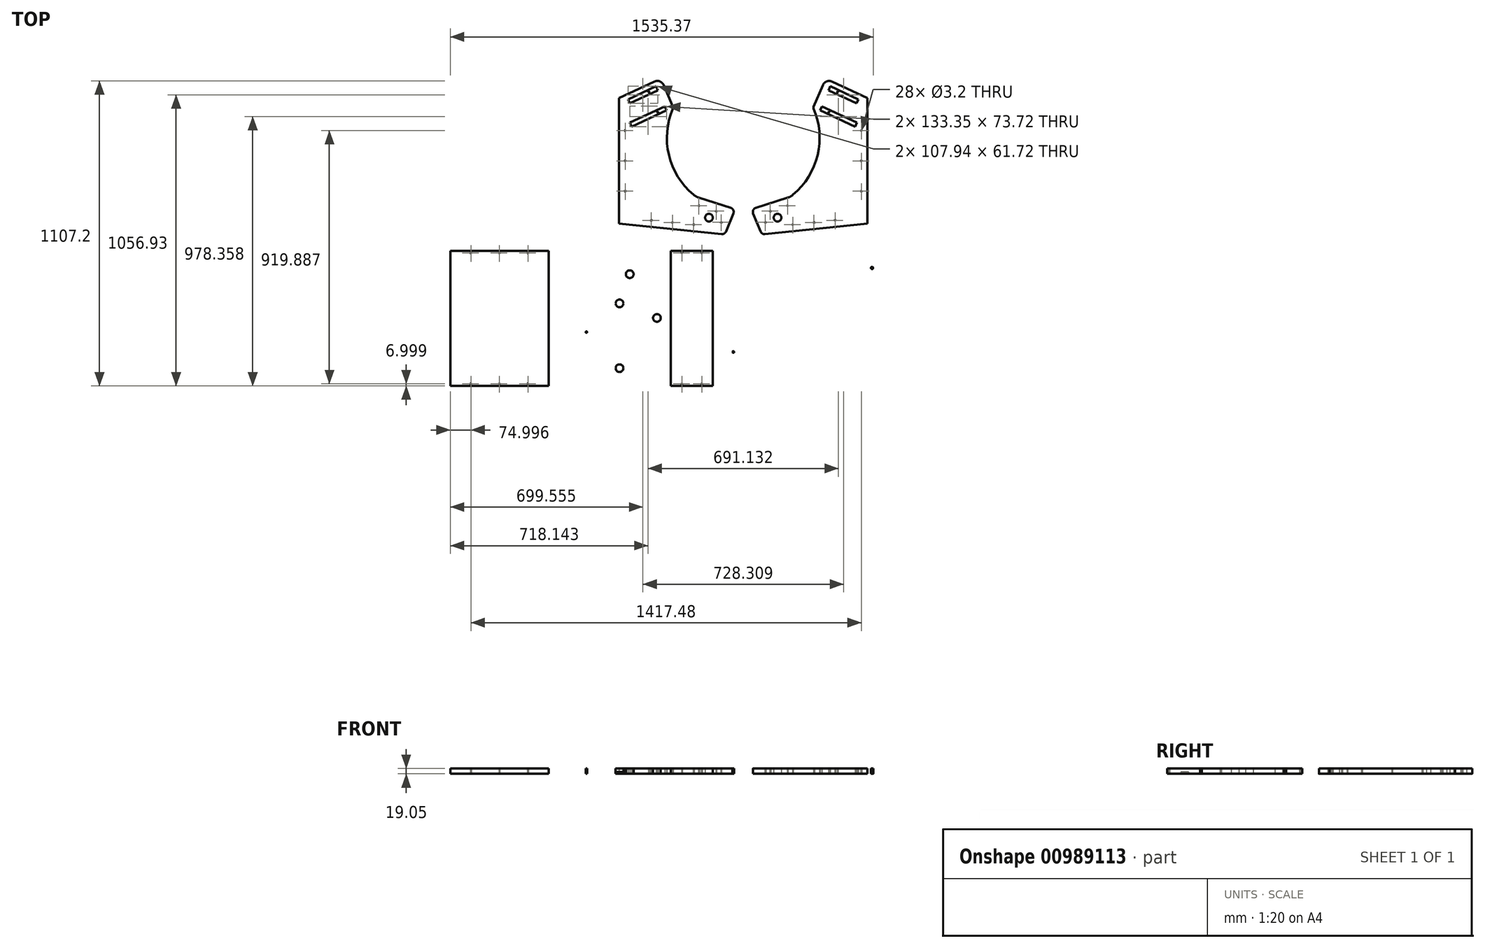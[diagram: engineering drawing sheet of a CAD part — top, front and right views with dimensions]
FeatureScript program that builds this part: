
annotation { "Feature Type Name" : "Feature", "Feature Type Description" : "" }
export const myFeature = defineFeature(function(context is Context, id is Id, definition is map)
    precondition{}
    {
        {
            var Q0;
            Q0=qCreatedBy(makeId("Top.planeOp"),FACE);
            var sketch = newSketch(context, id + "F0", { "sketchPlane" : qUnion([Q0])});
            skCircle(sketch, "E0", {"center": v(766.81, -125.45) * mm, "radius": 4 * mm});
            skCircle(sketch, "E1", {"center": v(417.5, -188.6) * mm, "radius": 5 * mm});
            skCircle(sketch, "E2", {"center": v(437.5, -188.6) * mm, "radius": 5 * mm});
            skCircle(sketch, "E3", {"center": v(417.5, -208.6) * mm, "radius": 5 * mm});
            skCircle(sketch, "E4", {"center": v(437.5, -208.6) * mm, "radius": 5 * mm});
            skCircle(sketch, "E5", {"center": v(417.5, -228.6) * mm, "radius": 5 * mm});
            skCircle(sketch, "E6", {"center": v(437.5, -228.6) * mm, "radius": 5 * mm});
            skCircle(sketch, "E7", {"center": v(437.5, -248.6) * mm, "radius": 5 * mm});
            skCircle(sketch, "E8", {"center": v(437.5, -288.6) * mm, "radius": 5 * mm});
            skCircle(sketch, "E9", {"center": v(437.5, -348.6) * mm, "radius": 5 * mm});
            skCircle(sketch, "E10", {"center": v(437.5, -328.6) * mm, "radius": 5 * mm});
            skCircle(sketch, "E11", {"center": v(437.5, -388.6) * mm, "radius": 5 * mm});
            skCircle(sketch, "E12", {"center": v(417.5, -368.6) * mm, "radius": 5 * mm});
            skCircle(sketch, "E13", {"center": v(417.5, -408.6) * mm, "radius": 5 * mm});
            skCircle(sketch, "E14", {"center": v(417.5, -428.6) * mm, "radius": 5 * mm});
            skCircle(sketch, "E15", {"center": v(437.5, -428.6) * mm, "radius": 5 * mm});
            skCircle(sketch, "E16", {"center": v(437.5, -408.6) * mm, "radius": 5 * mm});
            skLineSegment(sketch, "E17", {"start": v(355.37, -553.6) * mm, "end": v(805.37, -553.6) * mm});
            skLineSegment(sketch, "E18", {"start": v(805.37, -63.6) * mm, "end": v(355.37, -63.6) * mm});
            skLineSegment(sketch, "E19", {"start": v(355.37, -553.6) * mm, "end": v(355.37, -63.6) * mm});
            skCircle(sketch, "E20", {"center": v(457.5, -188.6) * mm, "radius": 5 * mm});
            skCircle(sketch, "E21", {"center": v(457.5, -208.6) * mm, "radius": 5 * mm});
            skCircle(sketch, "E22", {"center": v(457.5, -228.6) * mm, "radius": 5 * mm});
            skCircle(sketch, "E23", {"center": v(457.5, -248.6) * mm, "radius": 5 * mm});
            skCircle(sketch, "E24", {"center": v(457.5, -268.6) * mm, "radius": 5 * mm});
            skCircle(sketch, "E25", {"center": v(457.5, -328.6) * mm, "radius": 5 * mm});
            skCircle(sketch, "E26", {"center": v(457.5, -388.6) * mm, "radius": 5 * mm});
            skCircle(sketch, "E27", {"center": v(457.5, -368.6) * mm, "radius": 5 * mm});
            skCircle(sketch, "E28", {"center": v(457.5, -428.6) * mm, "radius": 5 * mm});
            skCircle(sketch, "E29", {"center": v(457.5, -408.6) * mm, "radius": 5 * mm});
            skCircle(sketch, "E30", {"center": v(-14.2, -307) * mm, "radius": 14 * mm});
            skCircle(sketch, "E31", {"center": v(-14.2, -373.6) * mm, "radius": 14 * mm});
            skLineSegment(sketch, "E32", {"start": v(-52.2, -63.6) * mm, "end": v(-52.2, -553.6) * mm});
            skLineSegment(sketch, "E33", {"start": v(23.8, -63.6) * mm, "end": v(23.8, -553.6) * mm});
            skCircle(sketch, "E34", {"center": v(263.18, -430.6) * mm, "radius": 3 * mm});
            skCircle(sketch, "E35", {"center": v(254.18, -430.6) * mm, "radius": 3 * mm});
            skCircle(sketch, "E36", {"center": v(245.18, -430.6) * mm, "radius": 3 * mm});
            skCircle(sketch, "E37", {"center": v(236.18, -430.6) * mm, "radius": 3 * mm});
            skCircle(sketch, "E38", {"center": v(227.18, -430.6) * mm, "radius": 3 * mm});
            skCircle(sketch, "E39", {"center": v(230.6, -413.38) * mm, "radius": 3 * mm});
            skCircle(sketch, "E40", {"center": v(240.36, -398.78) * mm, "radius": 3 * mm});
            skCircle(sketch, "E41", {"center": v(254.95, -389.03) * mm, "radius": 3 * mm});
            skCircle(sketch, "E42", {"center": v(272.18, -385.6) * mm, "radius": 3 * mm});
            skCircle(sketch, "E43", {"center": v(289.4, -389.03) * mm, "radius": 3 * mm});
            skCircle(sketch, "E44", {"center": v(304, -398.78) * mm, "radius": 3 * mm});
            skCircle(sketch, "E45", {"center": v(313.75, -413.38) * mm, "radius": 3 * mm});
            skCircle(sketch, "E46", {"center": v(317.18, -430.6) * mm, "radius": 3 * mm});
            skCircle(sketch, "E47", {"center": v(313.75, -447.82) * mm, "radius": 3 * mm});
            skCircle(sketch, "E48", {"center": v(304, -462.42) * mm, "radius": 3 * mm});
            skCircle(sketch, "E49", {"center": v(289.4, -472.18) * mm, "radius": 3 * mm});
            skCircle(sketch, "E50", {"center": v(272.18, -475.6) * mm, "radius": 3 * mm});
            skCircle(sketch, "E51", {"center": v(254.95, -472.18) * mm, "radius": 3 * mm});
            skCircle(sketch, "E52", {"center": v(240.36, -462.42) * mm, "radius": 3 * mm});
            skCircle(sketch, "E53", {"center": v(230.6, -447.82) * mm, "radius": 3 * mm});
            skCircle(sketch, "E54", {"center": v(308.18, -430.6) * mm, "radius": 3 * mm});
            skCircle(sketch, "E55", {"center": v(299.18, -430.6) * mm, "radius": 3 * mm});
            skCircle(sketch, "E56", {"center": v(290.18, -430.6) * mm, "radius": 3 * mm});
            skCircle(sketch, "E57", {"center": v(281.18, -430.6) * mm, "radius": 3 * mm});
            skCircle(sketch, "E58", {"center": v(272.18, -421.6) * mm, "radius": 3 * mm});
            skCircle(sketch, "E59", {"center": v(272.18, -412.6) * mm, "radius": 3 * mm});
            skCircle(sketch, "E60", {"center": v(272.18, -403.6) * mm, "radius": 3 * mm});
            skCircle(sketch, "E61", {"center": v(272.18, -394.6) * mm, "radius": 3 * mm});
            skCircle(sketch, "E62", {"center": v(272.18, -439.6) * mm, "radius": 3 * mm});
            skCircle(sketch, "E63", {"center": v(259.45, -443.33) * mm, "radius": 3 * mm});
            skCircle(sketch, "E64", {"center": v(247.23, -440.93) * mm, "radius": 3 * mm});
            skCircle(sketch, "E65", {"center": v(238.92, -444.38) * mm, "radius": 3 * mm});
            skCircle(sketch, "E66", {"center": v(272.18, -448.6) * mm, "radius": 3 * mm});
            skCircle(sketch, "E67", {"center": v(272.18, -457.6) * mm, "radius": 3 * mm});
            skCircle(sketch, "E68", {"center": v(272.18, -466.6) * mm, "radius": 3 * mm});
            skCircle(sketch, "E69", {"center": v(253.08, -449.7) * mm, "radius": 3 * mm});
            skCircle(sketch, "E70", {"center": v(246.72, -456.06) * mm, "radius": 3 * mm});
            skCircle(sketch, "E71", {"center": v(261.84, -455.55) * mm, "radius": 3 * mm});
            skCircle(sketch, "E72", {"center": v(258.4, -463.86) * mm, "radius": 3 * mm});
            skCircle(sketch, "E73", {"center": v(238.92, -416.82) * mm, "radius": 3 * mm});
            skCircle(sketch, "E74", {"center": v(247.23, -420.27) * mm, "radius": 3 * mm});
            skCircle(sketch, "E75", {"center": v(253.08, -411.5) * mm, "radius": 3 * mm});
            skCircle(sketch, "E76", {"center": v(259.45, -417.87) * mm, "radius": 3 * mm});
            skCircle(sketch, "E77", {"center": v(246.72, -405.15) * mm, "radius": 3 * mm});
            skCircle(sketch, "E78", {"center": v(258.4, -397.34) * mm, "radius": 3 * mm});
            skCircle(sketch, "E79", {"center": v(261.84, -405.66) * mm, "radius": 3 * mm});
            skCircle(sketch, "E80", {"center": v(285.95, -397.34) * mm, "radius": 3 * mm});
            skCircle(sketch, "E81", {"center": v(282.5, -405.66) * mm, "radius": 3 * mm});
            skCircle(sketch, "E82", {"center": v(291.27, -411.5) * mm, "radius": 3 * mm});
            skCircle(sketch, "E83", {"center": v(284.9, -417.87) * mm, "radius": 3 * mm});
            skCircle(sketch, "E84", {"center": v(297.63, -405.15) * mm, "radius": 3 * mm});
            skCircle(sketch, "E85", {"center": v(305.43, -416.82) * mm, "radius": 3 * mm});
            skCircle(sketch, "E86", {"center": v(297.12, -420.27) * mm, "radius": 3 * mm});
            skCircle(sketch, "E87", {"center": v(305.43, -444.38) * mm, "radius": 3 * mm});
            skCircle(sketch, "E88", {"center": v(297.12, -440.93) * mm, "radius": 3 * mm});
            skCircle(sketch, "E89", {"center": v(291.27, -449.7) * mm, "radius": 3 * mm});
            skCircle(sketch, "E90", {"center": v(284.9, -443.33) * mm, "radius": 3 * mm});
            skCircle(sketch, "E91", {"center": v(297.63, -456.06) * mm, "radius": 3 * mm});
            skCircle(sketch, "E92", {"center": v(285.95, -463.86) * mm, "radius": 3 * mm});
            skCircle(sketch, "E93", {"center": v(282.5, -455.55) * mm, "radius": 3 * mm});
            skCircle(sketch, "E94", {"center": v(263.18, -186.6) * mm, "radius": 3 * mm});
            skCircle(sketch, "E95", {"center": v(254.18, -186.6) * mm, "radius": 3 * mm});
            skCircle(sketch, "E96", {"center": v(245.18, -186.6) * mm, "radius": 3 * mm});
            skCircle(sketch, "E97", {"center": v(236.18, -186.6) * mm, "radius": 3 * mm});
            skCircle(sketch, "E98", {"center": v(227.18, -186.6) * mm, "radius": 3 * mm});
            skCircle(sketch, "E99", {"center": v(230.6, -169.38) * mm, "radius": 3 * mm});
            skCircle(sketch, "E100", {"center": v(240.36, -154.78) * mm, "radius": 3 * mm});
            skCircle(sketch, "E101", {"center": v(254.95, -145.03) * mm, "radius": 3 * mm});
            skCircle(sketch, "E102", {"center": v(272.18, -141.6) * mm, "radius": 3 * mm});
            skCircle(sketch, "E103", {"center": v(289.4, -145.03) * mm, "radius": 3 * mm});
            skCircle(sketch, "E104", {"center": v(304, -154.78) * mm, "radius": 3 * mm});
            skCircle(sketch, "E105", {"center": v(313.75, -169.38) * mm, "radius": 3 * mm});
            skCircle(sketch, "E106", {"center": v(317.18, -186.6) * mm, "radius": 3 * mm});
            skCircle(sketch, "E107", {"center": v(313.75, -203.82) * mm, "radius": 3 * mm});
            skCircle(sketch, "E108", {"center": v(304, -218.42) * mm, "radius": 3 * mm});
            skCircle(sketch, "E109", {"center": v(289.4, -228.18) * mm, "radius": 3 * mm});
            skCircle(sketch, "E110", {"center": v(272.18, -231.6) * mm, "radius": 3 * mm});
            skCircle(sketch, "E111", {"center": v(254.95, -228.18) * mm, "radius": 3 * mm});
            skCircle(sketch, "E112", {"center": v(240.36, -218.42) * mm, "radius": 3 * mm});
            skCircle(sketch, "E113", {"center": v(230.6, -203.82) * mm, "radius": 3 * mm});
            skCircle(sketch, "E114", {"center": v(308.18, -186.6) * mm, "radius": 3 * mm});
            skCircle(sketch, "E115", {"center": v(299.18, -186.6) * mm, "radius": 3 * mm});
            skCircle(sketch, "E116", {"center": v(290.18, -186.6) * mm, "radius": 3 * mm});
            skCircle(sketch, "E117", {"center": v(281.18, -186.6) * mm, "radius": 3 * mm});
            skCircle(sketch, "E118", {"center": v(272.18, -177.6) * mm, "radius": 3 * mm});
            skCircle(sketch, "E119", {"center": v(272.18, -168.6) * mm, "radius": 3 * mm});
            skCircle(sketch, "E120", {"center": v(272.18, -159.6) * mm, "radius": 3 * mm});
            skCircle(sketch, "E121", {"center": v(272.18, -150.6) * mm, "radius": 3 * mm});
            skCircle(sketch, "E122", {"center": v(272.18, -195.6) * mm, "radius": 3 * mm});
            skCircle(sketch, "E123", {"center": v(259.45, -199.33) * mm, "radius": 3 * mm});
            skCircle(sketch, "E124", {"center": v(247.23, -196.93) * mm, "radius": 3 * mm});
            skCircle(sketch, "E125", {"center": v(238.92, -200.38) * mm, "radius": 3 * mm});
            skCircle(sketch, "E126", {"center": v(272.18, -204.6) * mm, "radius": 3 * mm});
            skCircle(sketch, "E127", {"center": v(272.18, -213.6) * mm, "radius": 3 * mm});
            skCircle(sketch, "E128", {"center": v(272.18, -222.6) * mm, "radius": 3 * mm});
            skCircle(sketch, "E129", {"center": v(253.08, -205.7) * mm, "radius": 3 * mm});
            skCircle(sketch, "E130", {"center": v(246.72, -212.06) * mm, "radius": 3 * mm});
            skCircle(sketch, "E131", {"center": v(261.84, -211.55) * mm, "radius": 3 * mm});
            skCircle(sketch, "E132", {"center": v(258.4, -219.86) * mm, "radius": 3 * mm});
            skCircle(sketch, "E133", {"center": v(238.92, -172.82) * mm, "radius": 3 * mm});
            skCircle(sketch, "E134", {"center": v(247.23, -176.27) * mm, "radius": 3 * mm});
            skCircle(sketch, "E135", {"center": v(253.08, -167.5) * mm, "radius": 3 * mm});
            skCircle(sketch, "E136", {"center": v(259.45, -173.87) * mm, "radius": 3 * mm});
            skCircle(sketch, "E137", {"center": v(246.72, -161.15) * mm, "radius": 3 * mm});
            skCircle(sketch, "E138", {"center": v(258.4, -153.34) * mm, "radius": 3 * mm});
            skCircle(sketch, "E139", {"center": v(261.84, -161.66) * mm, "radius": 3 * mm});
            skCircle(sketch, "E140", {"center": v(285.95, -153.34) * mm, "radius": 3 * mm});
            skCircle(sketch, "E141", {"center": v(282.5, -161.66) * mm, "radius": 3 * mm});
            skCircle(sketch, "E142", {"center": v(291.27, -167.5) * mm, "radius": 3 * mm});
            skCircle(sketch, "E143", {"center": v(284.9, -173.87) * mm, "radius": 3 * mm});
            skCircle(sketch, "E144", {"center": v(297.63, -161.15) * mm, "radius": 3 * mm});
            skCircle(sketch, "E145", {"center": v(305.43, -172.82) * mm, "radius": 3 * mm});
            skCircle(sketch, "E146", {"center": v(297.12, -176.27) * mm, "radius": 3 * mm});
            skCircle(sketch, "E147", {"center": v(305.43, -200.38) * mm, "radius": 3 * mm});
            skCircle(sketch, "E148", {"center": v(297.12, -196.93) * mm, "radius": 3 * mm});
            skCircle(sketch, "E149", {"center": v(291.27, -205.7) * mm, "radius": 3 * mm});
            skCircle(sketch, "E150", {"center": v(284.9, -199.33) * mm, "radius": 3 * mm});
            skCircle(sketch, "E151", {"center": v(297.63, -212.06) * mm, "radius": 3 * mm});
            skCircle(sketch, "E152", {"center": v(285.95, -219.86) * mm, "radius": 3 * mm});
            skCircle(sketch, "E153", {"center": v(282.5, -211.55) * mm, "radius": 3 * mm});
            skLineSegment(sketch, "E154", {"start": v(201.18, -553.6) * mm, "end": v(201.18, -63.6) * mm});
            skLineSegment(sketch, "E155", {"start": v(343.18, -553.6) * mm, "end": v(343.18, -63.6) * mm});
            skLineSegment(sketch, "E156", {"start": v(-407.56, -63.6) * mm, "end": v(-764.56, -63.6) * mm});
            skLineSegment(sketch, "E157", {"start": v(-764.56, -553.6) * mm, "end": v(-407.56, -553.6) * mm});
            skLineSegment(sketch, "E158", {"start": v(-764.56, -553.6) * mm, "end": v(-764.56, -63.6) * mm});
            skLineSegment(sketch, "E159", {"start": v(-407.56, -553.6) * mm, "end": v(-407.56, -63.6) * mm});
            skArc(sketch, "E160", {"start": v(44.08, 453.91) * mm, "mid": v(44.7, 456.89) * mm, "end": v(44.08, 459.86) * mm});
            skArc(sketch, "E161", {"start": v(118.55, 140.38) * mm, "mid": v(128.17, 133.81) * mm, "end": v(138.89, 129.22) * mm});
            skArc(sketch, "E162", {"start": v(44.08, 453.91) * mm, "mid": v(29.27, 284.79) * mm, "end": v(118.55, 140.38) * mm});
            skArc(sketch, "E163", {"start": v(263.29, 72.7) * mm, "mid": v(263, 84.74) * mm, "end": v(253.95, 92.7) * mm});
            skLineSegment(sketch, "E164", {"start": v(138.89, 129.22) * mm, "end": v(253.95, 92.7) * mm});
            skArc(sketch, "E165", {"start": v(10.17, 538.5) * mm, "mid": v(-3.88, 551.96) * mm, "end": v(-23.32, 551.27) * mm});
            skArc(sketch, "E166", {"start": v(220.67, -2.68) * mm, "mid": v(229.91, -0.64) * mm, "end": v(236.1, 6.53) * mm});
            skLineSegment(sketch, "E167", {"start": v(44.08, 459.86) * mm, "end": v(10.17, 538.5) * mm});
            skLineSegment(sketch, "E168", {"start": v(-23.32, 551.27) * mm, "end": v(-152.11, 491.43) * mm});
            skLineSegment(sketch, "E169", {"start": v(263.29, 72.7) * mm, "end": v(236.1, 6.53) * mm});
            skLineSegment(sketch, "E170", {"start": v(-152.11, 491.43) * mm, "end": v(-152.11, 36) * mm});
            skLineSegment(sketch, "E171", {"start": v(220.67, -2.68) * mm, "end": v(-152.11, 36) * mm});
            skLineSegment(sketch, "E172", {"start": v(-395.37, -533.6) * mm, "end": v(-395.37, -518.6) * mm});
            skLineSegment(sketch, "E173", {"start": v(-245.37, -518.6) * mm, "end": v(-245.37, -533.6) * mm});
            skLineSegment(sketch, "E174", {"start": v(-245.37, -98.6) * mm, "end": v(-245.37, -83.6) * mm});
            skLineSegment(sketch, "E175", {"start": v(-395.37, -553.6) * mm, "end": v(-395.37, -63.6) * mm});
            skLineSegment(sketch, "E176", {"start": v(-245.37, -553.6) * mm, "end": v(-245.37, -63.6) * mm});
            skCircle(sketch, "E177", {"center": v(-270.37, -358.6) * mm, "radius": 2.5 * mm});
            skCircle(sketch, "E178", {"center": v(-270.37, -258.6) * mm, "radius": 2.5 * mm});
            skCircle(sketch, "E179", {"center": v(-370.37, -258.6) * mm, "radius": 2.5 * mm});
            skCircle(sketch, "E180", {"center": v(-370.37, -358.6) * mm, "radius": 2.5 * mm});
            skLineSegment(sketch, "E181", {"start": v(35.98, -553.6) * mm, "end": v(35.98, -63.6) * mm});
            skLineSegment(sketch, "E182", {"start": v(188.98, -63.6) * mm, "end": v(188.98, -553.6) * mm});
            skLineSegment(sketch, "E183", {"start": v(-395.37, -63.6) * mm, "end": v(-245.37, -63.6) * mm});
            skLineSegment(sketch, "E184", {"start": v(-245.37, -553.6) * mm, "end": v(-395.37, -553.6) * mm});
            skLineSegment(sketch, "E185", {"start": v(-52.2, -553.6) * mm, "end": v(23.8, -553.6) * mm});
            skLineSegment(sketch, "E186", {"start": v(23.8, -63.6) * mm, "end": v(-52.2, -63.6) * mm});
            skLineSegment(sketch, "E187", {"start": v(188.98, -553.6) * mm, "end": v(35.98, -553.6) * mm});
            skLineSegment(sketch, "E188", {"start": v(35.98, -63.6) * mm, "end": v(188.98, -63.6) * mm});
            skLineSegment(sketch, "E189", {"start": v(201.18, -63.6) * mm, "end": v(343.18, -63.6) * mm});
            skLineSegment(sketch, "E190", {"start": v(343.18, -553.6) * mm, "end": v(201.18, -553.6) * mm});
            skCircle(sketch, "E191", {"center": v(430.37, -71.1) * mm, "radius": 1.6 * mm});
            skCircle(sketch, "E192", {"center": v(698.37, -71.1) * mm, "radius": 1.6 * mm});
            skCircle(sketch, "E193", {"center": v(430.37, -546.1) * mm, "radius": 1.6 * mm});
            skCircle(sketch, "E194", {"center": v(730.37, -546.1) * mm, "radius": 1.6 * mm});
            skCircle(sketch, "E195", {"center": v(-689.56, -71.1) * mm, "radius": 1.6 * mm});
            skCircle(sketch, "E196", {"center": v(-482.56, -71.1) * mm, "radius": 1.6 * mm});
            skCircle(sketch, "E197", {"center": v(-689.56, -546.1) * mm, "radius": 1.6 * mm});
            skCircle(sketch, "E198", {"center": v(-482.56, -546.1) * mm, "radius": 1.6 * mm});
            skCircle(sketch, "E199", {"center": v(-43.24, 513.9) * mm, "radius": 1.6 * mm});
            skCircle(sketch, "E200", {"center": v(-87.02, 493.67) * mm, "radius": 1.6 * mm});
            skCircle(sketch, "E201", {"center": v(-11.55, 440.4) * mm, "radius": 1.6 * mm});
            skCircle(sketch, "E202", {"center": v(-80.97, 408.38) * mm, "radius": 1.6 * mm});
            skLineSegment(sketch, "E203", {"start": v(103.1, 119.6) * mm, "end": v(96.99, 104.75) * mm});
            skLineSegment(sketch, "E204", {"start": v(220.74, 63.9) * mm, "end": v(203.47, 21.86) * mm});
            skLineSegment(sketch, "E205", {"start": v(235.09, 59.34) * mm, "end": v(217.34, 16.16) * mm});
            skLineSegment(sketch, "E206", {"start": v(217.34, 16.16) * mm, "end": v(203.47, 21.86) * mm});
            skLineSegment(sketch, "E207", {"start": v(241.77, 75.58) * mm, "end": v(235.66, 60.73) * mm});
            skLineSegment(sketch, "E208", {"start": v(220.74, 63.9) * mm, "end": v(235.29, 59.27) * mm});
            skLineSegment(sketch, "E209", {"start": v(195.29, 16.04) * mm, "end": v(-112.17, 47.94) * mm});
            skLineSegment(sketch, "E210", {"start": v(103.1, 119.6) * mm, "end": v(241.77, 75.58) * mm});
            skLineSegment(sketch, "E211", {"start": v(-137.11, 473.55) * mm, "end": v(-137.11, 53.02) * mm});
            skLineSegment(sketch, "E212", {"start": v(-137.11, 53.02) * mm, "end": v(-121.11, 53.02) * mm});
            skLineSegment(sketch, "E213", {"start": v(196.94, 31.95) * mm, "end": v(195.29, 16.04) * mm});
            skLineSegment(sketch, "E214", {"start": v(-112.17, 47.94) * mm, "end": v(-110.52, 63.85) * mm});
            skLineSegment(sketch, "E215", {"start": v(-121.11, 473.55) * mm, "end": v(-137.11, 473.55) * mm});
            skLineSegment(sketch, "E216", {"start": v(-112.23, 472.47) * mm, "end": v(-118.98, 486.98) * mm});
            skLineSegment(sketch, "E217", {"start": v(-106.75, 387.9) * mm, "end": v(-113.1, 402.6) * mm});
            skLineSegment(sketch, "E218", {"start": v(-11.03, 519.5) * mm, "end": v(-17.37, 534.19) * mm});
            skLineSegment(sketch, "E219", {"start": v(20.26, 446.92) * mm, "end": v(-106.75, 387.9) * mm});
            skLineSegment(sketch, "E220", {"start": v(20.26, 446.92) * mm, "end": v(13.92, 461.62) * mm});
            skLineSegment(sketch, "E221", {"start": v(-17.37, 534.19) * mm, "end": v(-118.98, 486.98) * mm});
            skCircle(sketch, "E222", {"center": v(-129.61, 263.29) * mm, "radius": 1.6 * mm});
            skCircle(sketch, "E223", {"center": v(-129.61, 373.29) * mm, "radius": 1.6 * mm});
            skCircle(sketch, "E224", {"center": v(-129.61, 153.29) * mm, "radius": 1.6 * mm});
            skCircle(sketch, "E225", {"center": v(42.33, 39.45) * mm, "radius": 1.6 * mm});
            skCircle(sketch, "E226", {"center": v(-34.53, 47.42) * mm, "radius": 1.6 * mm});
            skCircle(sketch, "E227", {"center": v(119.22, 31.64) * mm, "radius": 1.6 * mm});
            skCircle(sketch, "E228", {"center": v(138.17, 100.6) * mm, "radius": 1.6 * mm});
            skCircle(sketch, "E229", {"center": v(200.98, 80.7) * mm, "radius": 1.6 * mm});
            skCircle(sketch, "E230", {"center": v(219.04, 40.02) * mm, "radius": 1.6 * mm});
            skArc(sketch, "E231", {"start": v(554.22, 459.86) * mm, "mid": v(553.6, 456.89) * mm, "end": v(554.22, 453.91) * mm});
            skArc(sketch, "E232", {"start": v(459.41, 129.22) * mm, "mid": v(470.13, 133.81) * mm, "end": v(479.75, 140.38) * mm});
            skArc(sketch, "E233", {"start": v(479.75, 140.38) * mm, "mid": v(569.03, 284.79) * mm, "end": v(554.22, 453.91) * mm});
            skArc(sketch, "E234", {"start": v(344.35, 92.7) * mm, "mid": v(335.3, 84.74) * mm, "end": v(335.01, 72.7) * mm});
            skLineSegment(sketch, "E235", {"start": v(459.41, 129.22) * mm, "end": v(344.35, 92.7) * mm});
            skArc(sketch, "E236", {"start": v(621.62, 551.27) * mm, "mid": v(602.17, 551.96) * mm, "end": v(588.13, 538.5) * mm});
            skArc(sketch, "E237", {"start": v(362.2, 6.53) * mm, "mid": v(368.39, -0.64) * mm, "end": v(377.63, -2.68) * mm});
            skLineSegment(sketch, "E238", {"start": v(554.22, 459.86) * mm, "end": v(588.13, 538.5) * mm});
            skLineSegment(sketch, "E239", {"start": v(621.62, 551.27) * mm, "end": v(750.41, 491.43) * mm});
            skLineSegment(sketch, "E240", {"start": v(335.01, 72.7) * mm, "end": v(362.2, 6.53) * mm});
            skLineSegment(sketch, "E241", {"start": v(750.41, 491.43) * mm, "end": v(750.41, 36) * mm});
            skLineSegment(sketch, "E242", {"start": v(377.63, -2.68) * mm, "end": v(750.41, 36) * mm});
            skCircle(sketch, "E243", {"center": v(-14.2, -70.6) * mm, "radius": 1.6 * mm});
            skCircle(sketch, "E244", {"center": v(-14.2, -546.6) * mm, "radius": 1.6 * mm});
            skCircle(sketch, "E245", {"center": v(236.18, -70.6) * mm, "radius": 1.6 * mm});
            skCircle(sketch, "E246", {"center": v(308.18, -70.6) * mm, "radius": 1.6 * mm});
            skCircle(sketch, "E247", {"center": v(236.18, -546.6) * mm, "radius": 1.6 * mm});
            skCircle(sketch, "E248", {"center": v(308.18, -546.6) * mm, "radius": 1.6 * mm});
            skCircle(sketch, "E249", {"center": v(76.48, -70.6) * mm, "radius": 1.6 * mm});
            skCircle(sketch, "E250", {"center": v(148.48, -70.6) * mm, "radius": 1.6 * mm});
            skCircle(sketch, "E251", {"center": v(76.48, -546.6) * mm, "radius": 1.6 * mm});
            skCircle(sketch, "E252", {"center": v(148.48, -546.6) * mm, "radius": 1.6 * mm});
            skCircle(sketch, "E253", {"center": v(174.76, 57.15) * mm, "radius": 14 * mm});
            skCircle(sketch, "E254", {"center": v(623.1, -256.1) * mm, "radius": 1.75 * mm});
            skCircle(sketch, "E255", {"center": v(623.1, -361.1) * mm, "radius": 1.75 * mm});
            skCircle(sketch, "E256", {"center": v(728.1, -361.1) * mm, "radius": 1.75 * mm});
            skCircle(sketch, "E257", {"center": v(728.1, -256.1) * mm, "radius": 1.75 * mm});
            skCircle(sketch, "E258", {"center": v(437.5, -308.6) * mm, "radius": 5 * mm});
            skCircle(sketch, "E259", {"center": v(457.5, -308.6) * mm, "radius": 5 * mm});
            skCircle(sketch, "E260", {"center": v(-586.06, -71.1) * mm, "radius": 1.6 * mm});
            skCircle(sketch, "E261", {"center": v(-586.06, -546.1) * mm, "radius": 1.6 * mm});
            skCircle(sketch, "E262", {"center": v(-150.03, -254.35) * mm, "radius": 14 * mm});
            skCircle(sketch, "E263", {"center": v(-113.03, -148.1) * mm, "radius": 14 * mm});
            skCircle(sketch, "E264", {"center": v(-153.03, -148.1) * mm, "radius": 14 * mm});
            skCircle(sketch, "E265", {"center": v(-131.03, -187.35) * mm, "radius": 14 * mm});
            skCircle(sketch, "E266", {"center": v(-171.03, -187.35) * mm, "radius": 14 * mm});
            skCircle(sketch, "E267", {"center": v(-113.03, -383.35) * mm, "radius": 14 * mm});
            skCircle(sketch, "E268", {"center": v(-153.03, -383.35) * mm, "radius": 14 * mm});
            skCircle(sketch, "E269", {"center": v(-131.03, -422.6) * mm, "radius": 14 * mm});
            skCircle(sketch, "E270", {"center": v(-171.03, -422.6) * mm, "radius": 14 * mm});
            skCircle(sketch, "E271", {"center": v(-150.03, -489.6) * mm, "radius": 14 * mm});
            skLineSegment(sketch, "E272", {"start": v(-64.03, -553.6) * mm, "end": v(-64.03, -63.6) * mm});
            skLineSegment(sketch, "E273", {"start": v(-64.03, -63.6) * mm, "end": v(-234.03, -63.6) * mm});
            skLineSegment(sketch, "E274", {"start": v(-234.03, -553.6) * mm, "end": v(-64.03, -553.6) * mm});
            skLineSegment(sketch, "E275", {"start": v(-234.03, -553.6) * mm, "end": v(-234.03, -63.6) * mm});
            skLineSegment(sketch, "E276", {"start": v(-101.03, -522.6) * mm, "end": v(-199.03, -522.6) * mm});
            skLineSegment(sketch, "E277", {"start": v(-199.03, -522.6) * mm, "end": v(-199.03, -456.6) * mm});
            skLineSegment(sketch, "E278", {"start": v(-199.03, -456.6) * mm, "end": v(-101.03, -456.6) * mm});
            skLineSegment(sketch, "E279", {"start": v(-101.03, -456.6) * mm, "end": v(-101.03, -522.6) * mm});
            skLineSegment(sketch, "E280", {"start": v(-101.03, -287.35) * mm, "end": v(-199.03, -287.35) * mm});
            skLineSegment(sketch, "E281", {"start": v(-199.03, -287.35) * mm, "end": v(-199.03, -221.35) * mm});
            skLineSegment(sketch, "E282", {"start": v(-199.03, -221.35) * mm, "end": v(-101.03, -221.35) * mm});
            skLineSegment(sketch, "E283", {"start": v(-101.03, -221.35) * mm, "end": v(-101.03, -287.35) * mm});
            skCircle(sketch, "E284", {"center": v(-99.03, -70.6) * mm, "radius": 1.6 * mm});
            skCircle(sketch, "E285", {"center": v(-199.03, -70.6) * mm, "radius": 1.6 * mm});
            skCircle(sketch, "E286", {"center": v(-99.03, -546.6) * mm, "radius": 1.6 * mm});
            skCircle(sketch, "E287", {"center": v(-199.03, -546.6) * mm, "radius": 1.6 * mm});
            skCircle(sketch, "E288", {"center": v(-113.03, -108.85) * mm, "radius": 14 * mm});
            skCircle(sketch, "E289", {"center": v(-153.03, -108.85) * mm, "radius": 14 * mm});
            skCircle(sketch, "E290", {"center": v(-113.03, -344.1) * mm, "radius": 14 * mm});
            skCircle(sketch, "E291", {"center": v(-153.03, -344.1) * mm, "radius": 14 * mm});
            skCircle(sketch, "E292", {"center": v(-14.2, -123.56) * mm, "radius": 14 * mm});
            skLineSegment(sketch, "E293", {"start": v(805.37, -553.6) * mm, "end": v(805.37, -63.6) * mm});
            skLineSegment(sketch, "E294", {"start": v(-11.03, 519.5) * mm, "end": v(-112.23, 472.47) * mm});
            skLineSegment(sketch, "E295", {"start": v(13.92, 461.62) * mm, "end": v(-113.1, 402.6) * mm});
            skLineSegment(sketch, "E296", {"start": v(-121.11, 473.55) * mm, "end": v(-121.11, 53.02) * mm});
            skLineSegment(sketch, "E297", {"start": v(196.94, 31.95) * mm, "end": v(-110.52, 63.85) * mm});
            skLineSegment(sketch, "E298", {"start": v(96.99, 104.75) * mm, "end": v(235.66, 60.73) * mm});
            skCircle(sketch, "E299", {"center": v(641.54, 513.9) * mm, "radius": 1.6 * mm});
            skCircle(sketch, "E300", {"center": v(685.32, 493.67) * mm, "radius": 1.6 * mm});
            skCircle(sketch, "E301", {"center": v(609.85, 440.4) * mm, "radius": 1.6 * mm});
            skCircle(sketch, "E302", {"center": v(679.27, 408.38) * mm, "radius": 1.6 * mm});
            skLineSegment(sketch, "E303", {"start": v(495.2, 119.6) * mm, "end": v(501.31, 104.75) * mm});
            skLineSegment(sketch, "E304", {"start": v(377.55, 63.9) * mm, "end": v(394.83, 21.86) * mm});
            skLineSegment(sketch, "E305", {"start": v(363.2, 59.34) * mm, "end": v(380.96, 16.16) * mm});
            skLineSegment(sketch, "E306", {"start": v(380.96, 16.16) * mm, "end": v(394.83, 21.86) * mm});
            skLineSegment(sketch, "E307", {"start": v(356.53, 75.58) * mm, "end": v(362.64, 60.73) * mm});
            skLineSegment(sketch, "E308", {"start": v(377.55, 63.9) * mm, "end": v(363.01, 59.27) * mm});
            skLineSegment(sketch, "E309", {"start": v(403.01, 16.04) * mm, "end": v(710.46, 47.94) * mm});
            skLineSegment(sketch, "E310", {"start": v(401.36, 31.95) * mm, "end": v(708.81, 63.85) * mm});
            skLineSegment(sketch, "E311", {"start": v(501.31, 104.75) * mm, "end": v(362.64, 60.73) * mm});
            skLineSegment(sketch, "E312", {"start": v(495.2, 119.6) * mm, "end": v(356.53, 75.58) * mm});
            skLineSegment(sketch, "E313", {"start": v(735.41, 473.55) * mm, "end": v(735.41, 53.02) * mm});
            skLineSegment(sketch, "E314", {"start": v(719.41, 473.55) * mm, "end": v(719.41, 53.02) * mm});
            skLineSegment(sketch, "E315", {"start": v(735.41, 53.02) * mm, "end": v(719.41, 53.02) * mm});
            skLineSegment(sketch, "E316", {"start": v(401.36, 31.95) * mm, "end": v(403.01, 16.04) * mm});
            skLineSegment(sketch, "E317", {"start": v(710.46, 47.94) * mm, "end": v(708.81, 63.85) * mm});
            skLineSegment(sketch, "E318", {"start": v(719.41, 473.55) * mm, "end": v(735.41, 473.55) * mm});
            skLineSegment(sketch, "E319", {"start": v(710.53, 472.47) * mm, "end": v(717.27, 486.98) * mm});
            skLineSegment(sketch, "E320", {"start": v(705.05, 387.9) * mm, "end": v(711.39, 402.6) * mm});
            skLineSegment(sketch, "E321", {"start": v(609.33, 519.5) * mm, "end": v(615.67, 534.19) * mm});
            skLineSegment(sketch, "E322", {"start": v(609.33, 519.5) * mm, "end": v(710.53, 472.47) * mm});
            skLineSegment(sketch, "E323", {"start": v(578.04, 446.92) * mm, "end": v(705.05, 387.9) * mm});
            skLineSegment(sketch, "E324", {"start": v(584.38, 461.62) * mm, "end": v(711.39, 402.6) * mm});
            skLineSegment(sketch, "E325", {"start": v(578.04, 446.92) * mm, "end": v(584.38, 461.62) * mm});
            skLineSegment(sketch, "E326", {"start": v(615.67, 534.19) * mm, "end": v(717.27, 486.98) * mm});
            skCircle(sketch, "E327", {"center": v(727.91, 263.29) * mm, "radius": 1.6 * mm});
            skCircle(sketch, "E328", {"center": v(727.91, 373.29) * mm, "radius": 1.6 * mm});
            skCircle(sketch, "E329", {"center": v(727.91, 153.29) * mm, "radius": 1.6 * mm});
            skCircle(sketch, "E330", {"center": v(555.96, 39.45) * mm, "radius": 1.6 * mm});
            skCircle(sketch, "E331", {"center": v(632.83, 47.42) * mm, "radius": 1.6 * mm});
            skCircle(sketch, "E332", {"center": v(479.08, 31.64) * mm, "radius": 1.6 * mm});
            skCircle(sketch, "E333", {"center": v(460.13, 100.6) * mm, "radius": 1.6 * mm});
            skCircle(sketch, "E334", {"center": v(397.32, 80.7) * mm, "radius": 1.6 * mm});
            skCircle(sketch, "E335", {"center": v(379.26, 40.02) * mm, "radius": 1.6 * mm});
            skCircle(sketch, "E336", {"center": v(423.54, 57.15) * mm, "radius": 14 * mm});
            skCircle(sketch, "E337", {"center": v(417.5, -268.6) * mm, "radius": 5 * mm});
            skCircle(sketch, "E338", {"center": v(417.5, -288.6) * mm, "radius": 5 * mm});
            skCircle(sketch, "E339", {"center": v(417.5, -348.6) * mm, "radius": 5 * mm});
            skCircle(sketch, "E340", {"center": v(417.5, -328.6) * mm, "radius": 5 * mm});
            skCircle(sketch, "E341", {"center": v(417.5, -308.6) * mm, "radius": 5 * mm});
            skCircle(sketch, "E342", {"center": v(477.5, -208.6) * mm, "radius": 5 * mm});
            skCircle(sketch, "E343", {"center": v(477.5, -228.6) * mm, "radius": 5 * mm});
            skCircle(sketch, "E344", {"center": v(477.5, -248.6) * mm, "radius": 5 * mm});
            skCircle(sketch, "E345", {"center": v(477.5, -268.6) * mm, "radius": 5 * mm});
            skCircle(sketch, "E346", {"center": v(477.5, -288.6) * mm, "radius": 5 * mm});
            skCircle(sketch, "E347", {"center": v(477.5, -348.6) * mm, "radius": 5 * mm});
            skCircle(sketch, "E348", {"center": v(477.5, -388.6) * mm, "radius": 5 * mm});
            skCircle(sketch, "E349", {"center": v(477.5, -368.6) * mm, "radius": 5 * mm});
            skCircle(sketch, "E350", {"center": v(477.5, -408.6) * mm, "radius": 5 * mm});
            skCircle(sketch, "E351", {"center": v(497.5, -248.6) * mm, "radius": 5 * mm});
            skCircle(sketch, "E352", {"center": v(497.5, -268.6) * mm, "radius": 5 * mm});
            skCircle(sketch, "E353", {"center": v(497.5, -388.6) * mm, "radius": 5 * mm});
            skCircle(sketch, "E354", {"center": v(497.5, -368.6) * mm, "radius": 5 * mm});
            skCircle(sketch, "E355", {"center": v(417.5, -148.6) * mm, "radius": 5 * mm});
            skCircle(sketch, "E356", {"center": v(417.5, -168.6) * mm, "radius": 5 * mm});
            skCircle(sketch, "E357", {"center": v(437.5, -168.6) * mm, "radius": 5 * mm});
            skCircle(sketch, "E358", {"center": v(417.5, -448.6) * mm, "radius": 5 * mm});
            skCircle(sketch, "E359", {"center": v(417.5, -468.6) * mm, "radius": 5 * mm});
            skCircle(sketch, "E360", {"center": v(437.5, -448.6) * mm, "radius": 5 * mm});
            skFitSpline(sketch, "E361", {"points": [v(675.84, -253.54) * mm, v(678.69, -256.9) * mm, v(685.24, -264.62) * mm, v(676.96, -275.84) * mm, v(680.6, -283.86) * mm, v(677.66, -287.66) * mm, v(676.38, -288.34) * mm]});
            skFitSpline(sketch, "E362", {"points": [v(676.38, -288.34) * mm, v(676.19, -288.44) * mm, v(673.55, -289.44) * mm, v(673.4, -275.49) * mm, v(668.83, -265.8) * mm, v(673.52, -257.6) * mm, v(675.84, -253.54) * mm]});
            skFitSpline(sketch, "E363", {"points": [v(657, -256.78) * mm, v(660.82, -258.96) * mm, v(669.62, -263.98) * mm, v(665.67, -277.35) * mm, v(671.84, -283.64) * mm, v(670.38, -288.22) * mm, v(669.4, -289.3) * mm]});
            skFitSpline(sketch, "E364", {"points": [v(669.4, -289.3) * mm, v(669.26, -289.46) * mm, v(667.12, -291.3) * mm, v(662.2, -278.24) * mm, v(654.6, -270.7) * mm, v(656.2, -261.39) * mm, v(657, -256.78) * mm]});
            skFitSpline(sketch, "E365", {"points": [v(640.4, -266.27) * mm, v(644.73, -267.01) * mm, v(654.72, -268.72) * mm, v(655.58, -282.63) * mm, v(663.53, -286.44) * mm, v(663.72, -291.24) * mm, v(663.17, -292.59) * mm]});
            skFitSpline(sketch, "E366", {"points": [v(663.17, -292.59) * mm, v(663.1, -292.78) * mm, v(661.72, -295.24) * mm, v(652.63, -284.65) * mm, v(642.9, -280.18) * mm, v(641.22, -270.87) * mm, v(640.4, -266.27) * mm]});
            skFitSpline(sketch, "E367", {"points": [v(628.04, -280.87) * mm, v(632.37, -280.08) * mm, v(642.34, -278.27) * mm, v(647.9, -291.05) * mm, v(656.68, -291.9) * mm, v(658.5, -296.35) * mm, v(658.44, -297.8) * mm]});
            skFitSpline(sketch, "E368", {"points": [v(658.44, -297.8) * mm, v(658.43, -298.02) * mm, v(657.98, -300.8) * mm, v(645.83, -293.96) * mm, v(635.16, -293.08) * mm, v(630.4, -284.91) * mm, v(628.04, -280.87) * mm]});
            skFitSpline(sketch, "E369", {"points": [v(621.42, -298.81) * mm, v(625.22, -296.6) * mm, v(633.97, -291.48) * mm, v(643.58, -301.58) * mm, v(652.1, -299.39) * mm, v(655.34, -302.94) * mm, v(655.79, -304.33) * mm]});
            skFitSpline(sketch, "E370", {"points": [v(655.79, -304.33) * mm, v(655.85, -304.53) * mm, v(656.38, -307.3) * mm, v(642.61, -305.03) * mm, v(632.29, -307.85) * mm, v(625.02, -301.8) * mm, v(621.42, -298.81) * mm]});
            skFitSpline(sketch, "E371", {"points": [v(621.34, -317.94) * mm, v(624.15, -314.55) * mm, v(630.62, -306.75) * mm, v(643.1, -312.96) * mm, v(650.37, -307.98) * mm, v(654.63, -310.22) * mm, v(655.52, -311.36) * mm]});
            skFitSpline(sketch, "E372", {"points": [v(655.52, -311.36) * mm, v(655.65, -311.53) * mm, v(657.1, -313.95) * mm, v(643.38, -316.53) * mm, v(634.64, -322.71) * mm, v(625.74, -319.52) * mm, v(621.34, -317.94) * mm]});
            skFitSpline(sketch, "E373", {"points": [v(627.8, -335.93) * mm, v(629.3, -331.79) * mm, v(632.7, -322.25) * mm, v(646.56, -323.81) * mm, v(651.68, -316.65) * mm, v(656.45, -317.3) * mm, v(657.68, -318.07) * mm]});
            skFitSpline(sketch, "E374", {"points": [v(657.68, -318.07) * mm, v(657.86, -318.18) * mm, v(660.04, -319.96) * mm, v(648.03, -327.07) * mm, v(641.94, -335.87) * mm, v(632.48, -335.91) * mm, v(627.8, -335.93) * mm]});
            skFitSpline(sketch, "E375", {"points": [v(640.04, -350.63) * mm, v(640.01, -346.23) * mm, v(639.96, -336.1) * mm, v(653.5, -332.83) * mm, v(655.88, -324.35) * mm, v(660.57, -323.32) * mm, v(662, -323.63) * mm]});
            skFitSpline(sketch, "E376", {"points": [v(662, -323.63) * mm, v(662.2, -323.68) * mm, v(664.87, -324.6) * mm, v(656.01, -335.39) * mm, v(653.3, -345.74) * mm, v(644.43, -349.02) * mm, v(640.04, -350.63) * mm]});
            skFitSpline(sketch, "E377", {"points": [v(656.56, -360.26) * mm, v(655.03, -356.14) * mm, v(651.51, -346.63) * mm, v(663.13, -338.93) * mm, v(662.45, -330.14) * mm, v(666.52, -327.58) * mm, v(667.96, -327.38) * mm]});
            skFitSpline(sketch, "E378", {"points": [v(667.96, -327.38) * mm, v(668.17, -327.35) * mm, v(670.99, -327.31) * mm, v(666.36, -340.47) * mm, v(667.34, -351.13) * mm, v(660.13, -357.24) * mm, v(656.56, -360.26) * mm]});
            skFitSpline(sketch, "E379", {"points": [v(675.38, -363.66) * mm, v(672.53, -360.3) * mm, v(665.97, -352.58) * mm, v(674.25, -341.37) * mm, v(670.61, -333.34) * mm, v(673.55, -329.54) * mm, v(674.84, -328.86) * mm]});
            skFitSpline(sketch, "E380", {"points": [v(674.84, -328.86) * mm, v(675.03, -328.77) * mm, v(677.66, -327.76) * mm, v(677.82, -341.72) * mm, v(682.4, -351.4) * mm, v(677.7, -359.6) * mm, v(675.38, -363.66) * mm]});
            skFitSpline(sketch, "E381", {"points": [v(694.23, -360.42) * mm, v(690.4, -358.24) * mm, v(681.6, -353.22) * mm, v(685.54, -339.85) * mm, v(679.38, -333.56) * mm, v(680.84, -328.98) * mm, v(681.82, -327.9) * mm]});
            skFitSpline(sketch, "E382", {"points": [v(681.82, -327.9) * mm, v(681.96, -327.75) * mm, v(684.1, -325.9) * mm, v(689, -338.96) * mm, v(696.62, -346.5) * mm, v(695.02, -355.81) * mm, v(694.23, -360.42) * mm]});
            skFitSpline(sketch, "E383", {"points": [v(710.83, -350.93) * mm, v(706.49, -350.19) * mm, v(696.5, -348.49) * mm, v(695.63, -334.57) * mm, v(687.69, -330.77) * mm, v(687.5, -325.96) * mm, v(688.05, -324.62) * mm]});
            skFitSpline(sketch, "E384", {"points": [v(688.05, -324.62) * mm, v(688.13, -324.42) * mm, v(689.5, -321.96) * mm, v(698.59, -332.55) * mm, v(708.31, -337.02) * mm, v(710, -346.33) * mm, v(710.83, -350.93) * mm]});
            skFitSpline(sketch, "E385", {"points": [v(723.18, -336.33) * mm, v(718.85, -337.12) * mm, v(708.88, -338.94) * mm, v(703.3, -326.16) * mm, v(694.54, -325.3) * mm, v(692.72, -320.85) * mm, v(692.77, -319.4) * mm]});
            skFitSpline(sketch, "E386", {"points": [v(692.77, -319.4) * mm, v(692.78, -319.19) * mm, v(693.23, -316.4) * mm, v(705.4, -323.25) * mm, v(716.06, -324.12) * mm, v(720.82, -332.3) * mm, v(723.18, -336.33) * mm]});
            skFitSpline(sketch, "E387", {"points": [v(729.8, -318.39) * mm, v(726, -320.61) * mm, v(717.25, -325.73) * mm, v(707.64, -315.62) * mm, v(699.1, -317.82) * mm, v(695.87, -314.26) * mm, v(695.43, -312.88) * mm]});
            skFitSpline(sketch, "E388", {"points": [v(695.43, -312.88) * mm, v(695.37, -312.67) * mm, v(694.84, -309.9) * mm, v(708.6, -312.18) * mm, v(718.93, -309.35) * mm, v(726.2, -315.4) * mm, v(729.8, -318.39) * mm]});
            skFitSpline(sketch, "E389", {"points": [v(729.87, -299.27) * mm, v(727.06, -302.65) * mm, v(720.6, -310.45) * mm, v(708.11, -304.25) * mm, v(700.84, -309.22) * mm, v(696.59, -306.99) * mm, v(695.7, -305.84) * mm]});
            skFitSpline(sketch, "E390", {"points": [v(695.7, -305.84) * mm, v(695.57, -305.67) * mm, v(694.12, -303.25) * mm, v(707.84, -300.68) * mm, v(716.57, -294.5) * mm, v(725.47, -297.69) * mm, v(729.87, -299.27) * mm]});
            skFitSpline(sketch, "E391", {"points": [v(723.4, -281.27) * mm, v(721.93, -285.41) * mm, v(718.51, -294.96) * mm, v(704.66, -293.4) * mm, v(699.53, -300.55) * mm, v(694.77, -299.9) * mm, v(693.54, -299.13) * mm]});
            skFitSpline(sketch, "E392", {"points": [v(693.54, -299.13) * mm, v(693.36, -299.02) * mm, v(691.17, -297.24) * mm, v(703.18, -290.13) * mm, v(709.28, -281.33) * mm, v(718.73, -281.29) * mm, v(723.4, -281.27) * mm]});
            skFitSpline(sketch, "E393", {"points": [v(711.18, -266.57) * mm, v(711.2, -270.97) * mm, v(711.26, -281.1) * mm, v(697.7, -284.37) * mm, v(695.34, -292.86) * mm, v(690.64, -293.88) * mm, v(689.22, -293.57) * mm]});
            skFitSpline(sketch, "E394", {"points": [v(689.22, -293.57) * mm, v(689.01, -293.53) * mm, v(686.35, -292.6) * mm, v(695.2, -281.81) * mm, v(697.92, -271.46) * mm, v(706.8, -268.19) * mm, v(711.18, -266.57) * mm]});
            skFitSpline(sketch, "E395", {"points": [v(694.66, -256.94) * mm, v(696.18, -261.07) * mm, v(699.7, -270.57) * mm, v(688.09, -278.28) * mm, v(688.76, -287.06) * mm, v(684.7, -289.63) * mm, v(683.26, -289.82) * mm]});
            skFitSpline(sketch, "E396", {"points": [v(683.26, -289.82) * mm, v(683.05, -289.85) * mm, v(680.23, -289.9) * mm, v(684.86, -276.73) * mm, v(683.87, -266.07) * mm, v(691.09, -259.96) * mm, v(694.66, -256.94) * mm]});
            skLineSegment(sketch, "E397.bottom", {"start": v(772.18, -366.33) * mm, "end": v(767.52, -366.33) * mm});
            skLineSegment(sketch, "E397.top", {"start": v(772.18, -250.87) * mm, "end": v(767.52, -250.87) * mm});
            skLineSegment(sketch, "E397.left", {"start": v(784.88, -353.63) * mm, "end": v(784.88, -263.57) * mm});
            skLineSegment(sketch, "E397.right", {"start": v(754.82, -353.63) * mm, "end": v(754.82, -263.57) * mm});
            skPoint(sketch, "E397.middle", {"position": v(769.85, -308.6) * mm});
            skPoint(sketch, "E397.middle.positionSnap0", {"position": v(805.37, -308.6) * mm});
            skPoint(sketch, "E397.centerSnap0", {"position": v(805.37, -308.6) * mm});
            skPoint(sketch, "E398.visualSharp", {"position": v(784.88, -250.87) * mm});
            skArc(sketch, "E398.filletArc", {"start": v(784.88, -263.57) * mm, "mid": v(781.16, -254.6) * mm, "end": v(772.18, -250.87) * mm});
            skPoint(sketch, "E399.visualSharp", {"position": v(784.88, -366.33) * mm});
            skArc(sketch, "E399.filletArc", {"start": v(772.18, -366.33) * mm, "mid": v(781.16, -362.61) * mm, "end": v(784.88, -353.63) * mm});
            skPoint(sketch, "E400.visualSharp", {"position": v(754.82, -250.87) * mm});
            skArc(sketch, "E400.filletArc", {"start": v(767.52, -250.87) * mm, "mid": v(758.54, -254.6) * mm, "end": v(754.82, -263.57) * mm});
            skPoint(sketch, "E401.visualSharp", {"position": v(754.82, -366.33) * mm});
            skArc(sketch, "E401.filletArc", {"start": v(754.82, -353.63) * mm, "mid": v(758.54, -362.61) * mm, "end": v(767.52, -366.33) * mm});
            skLineSegment(sketch, "E402.bottom", {"start": v(413.13, -517.23) * mm, "end": v(463.1, -517.23) * mm});
            skLineSegment(sketch, "E402.top", {"start": v(413.13, -489.09) * mm, "end": v(463.1, -489.09) * mm});
            skLineSegment(sketch, "E402.left", {"start": v(413.13, -517.23) * mm, "end": v(413.13, -489.09) * mm});
            skLineSegment(sketch, "E402.right", {"start": v(463.1, -517.23) * mm, "end": v(463.1, -489.09) * mm});
            skSolve(sketch);
        }
        {
            var Q0;
            Q0=makeQuery(id+"F0.imprint","IMPRINT",FACE,{"disambiguationData":[TD([[makeQuery(id+"F0.imprint","IMPRINT",EDGE,{"derivedFrom":sQuery(id+"F0.wireOp",EDGE,"E160")}),1.0]])]});
            var Q1;
            Q1=makeQuery(id+"F0.imprint","IMPRINT",FACE,{"disambiguationData":[TD([[makeQuery(id+"F0.imprint","IMPRINT",EDGE,{"derivedFrom":sQuery(id+"F0.wireOp",EDGE,"E211")}),1.0]])]});
            var Q2;
            Q2=makeQuery(id+"F0.imprint","IMPRINT",FACE,{"disambiguationData":[TD([[makeQuery(id+"F0.imprint","IMPRINT",EDGE,{"derivedFrom":sQuery(id+"F0.wireOp",EDGE,"E201")}),1.0]])]});
            var Q3;
            Q3=makeQuery(id+"F0.imprint","IMPRINT",FACE,{"disambiguationData":[TD([[makeQuery(id+"F0.imprint","IMPRINT",EDGE,{"derivedFrom":sQuery(id+"F0.wireOp",EDGE,"E199")}),1.0]])]});
            var Q4;
            {var subQ1=sQuery(id+"F0.wireOp",EDGE,"E204");Q4=makeQuery(id+"F0.imprint","IMPRINT",FACE,{"disambiguationData":[TD([[makeQuery(id+"F0.imprint","IMPRINT",EDGE,{"derivedFrom":subQ1}),1.0]])]});}
            var Q5;
            Q5=makeQuery(id+"F0.imprint","IMPRINT",FACE,{"disambiguationData":[TD([[makeQuery(id+"F0.imprint","IMPRINT",EDGE,{"derivedFrom":sQuery(id+"F0.wireOp",EDGE,"E203")}),1.0]])]});
            var Q6;
            Q6=makeQuery(id+"F0.imprint","IMPRINT",FACE,{"disambiguationData":[TD([[makeQuery(id+"F0.imprint","IMPRINT",EDGE,{"derivedFrom":sQuery(id+"F0.wireOp",EDGE,"E253")}),-1.0]])]});
            var Q7;
            Q7=makeQuery(id+"F0.imprint","IMPRINT",FACE,{"disambiguationData":[TD([[makeQuery(id+"F0.imprint","IMPRINT",EDGE,{"derivedFrom":sQuery(id+"F0.wireOp",EDGE,"E209")}),-1.0]])]});
            extrude(context, id + "F1", {"entities" : qUnion([Q0, Q1, Q2, Q3, Q4, Q5, Q6, Q7]), "depth" : 19.05 * mm, "offsetDistance" : 25.4 * mm});
        }
        {
            var Q0;
            Q0=makeQuery(id+"F0.imprint","IMPRINT",FACE,{"disambiguationData":[TD([[makeQuery(id+"F0.imprint","IMPRINT",EDGE,{"derivedFrom":sQuery(id+"F0.wireOp",EDGE,"E231")}),1.0]])]});
            var Q1;
            Q1=makeQuery(id+"F0.imprint","IMPRINT",FACE,{"disambiguationData":[TD([[makeQuery(id+"F0.imprint","IMPRINT",EDGE,{"derivedFrom":sQuery(id+"F0.wireOp",EDGE,"E299")}),1.0]])]});
            var Q2;
            Q2=makeQuery(id+"F0.imprint","IMPRINT",FACE,{"disambiguationData":[TD([[makeQuery(id+"F0.imprint","IMPRINT",EDGE,{"derivedFrom":sQuery(id+"F0.wireOp",EDGE,"E301")}),1.0]])]});
            var Q3;
            Q3=makeQuery(id+"F0.imprint","IMPRINT",FACE,{"disambiguationData":[TD([[makeQuery(id+"F0.imprint","IMPRINT",EDGE,{"derivedFrom":sQuery(id+"F0.wireOp",EDGE,"E313")}),-1.0]])]});
            var Q4;
            Q4=makeQuery(id+"F0.imprint","IMPRINT",FACE,{"disambiguationData":[TD([[makeQuery(id+"F0.imprint","IMPRINT",EDGE,{"derivedFrom":sQuery(id+"F0.wireOp",EDGE,"E303")}),-1.0]])]});
            var Q5;
            Q5=makeQuery(id+"F0.imprint","IMPRINT",FACE,{"disambiguationData":[TD([[makeQuery(id+"F0.imprint","IMPRINT",EDGE,{"derivedFrom":sQuery(id+"F0.wireOp",EDGE,"E336")}),-1.0]])]});
            var Q6;
            {var subQ1=sQuery(id+"F0.wireOp",EDGE,"E304");Q6=makeQuery(id+"F0.imprint","IMPRINT",FACE,{"disambiguationData":[TD([[makeQuery(id+"F0.imprint","IMPRINT",EDGE,{"derivedFrom":subQ1}),-1.0]])]});}
            var Q7;
            Q7=makeQuery(id+"F0.imprint","IMPRINT",FACE,{"disambiguationData":[TD([[makeQuery(id+"F0.imprint","IMPRINT",EDGE,{"derivedFrom":sQuery(id+"F0.wireOp",EDGE,"E309")}),1.0]])]});
            extrude(context, id + "F2", {"entities" : qUnion([Q0, Q1, Q2, Q3, Q4, Q5, Q6, Q7]), "depth" : 19.05 * mm, "offsetDistance" : 25.4 * mm});
        }
        {
            var Q0;
            Q0=makeQuery(id+"F0.imprint","IMPRINT",FACE,{"disambiguationData":[TD([[makeQuery(id+"F0.imprint","IMPRINT",EDGE,{"derivedFrom":sQuery(id+"F0.wireOp",EDGE,"E156")}),1.0]])]});
            extrude(context, id + "F3", {"entities" : qUnion([Q0]), "depth" : 19.05 * mm, "offsetDistance" : 25.4 * mm});
        }
        {
            var Q0;
            Q0=makeQuery(id+"F0.imprint","IMPRINT",FACE,{"disambiguationData":[TD([[makeQuery(id+"F0.imprint","IMPRINT",EDGE,{"derivedFrom":sQuery(id+"F0.wireOp",EDGE,"E177")}),1.0]])]});
            extrude(context, id + "F4", {"entities" : qUnion([Q0]), "depth" : 19.05 * mm, "offsetDistance" : 25.4 * mm});
        }
        {
            var Q0;
            Q0=makeQuery(id+"F0.imprint","IMPRINT",FACE,{"disambiguationData":[TD([[makeQuery(id+"F0.imprint","IMPRINT",EDGE,{"derivedFrom":sQuery(id+"F0.wireOp",EDGE,"E263")}),1.0]])]});
            var Q1;
            Q1=makeQuery(id+"F0.imprint","IMPRINT",FACE,{"disambiguationData":[TD([[makeQuery(id+"F0.imprint","IMPRINT",EDGE,{"derivedFrom":sQuery(id+"F0.wireOp",EDGE,"E262")}),1.0]])]});
            var Q2;
            Q2=makeQuery(id+"F0.imprint","IMPRINT",FACE,{"disambiguationData":[TD([[makeQuery(id+"F0.imprint","IMPRINT",EDGE,{"derivedFrom":sQuery(id+"F0.wireOp",EDGE,"E271")}),1.0]])]});
            extrude(context, id + "F5", {"entities" : qUnion([Q0, Q1, Q2]), "depth" : 19.05 * mm, "offsetDistance" : 25.4 * mm});
        }
        {
            var Q0;
            Q0=makeQuery(id+"F0.imprint","IMPRINT",FACE,{"disambiguationData":[TD([[makeQuery(id+"F0.imprint","IMPRINT",EDGE,{"derivedFrom":sQuery(id+"F0.wireOp",EDGE,"E181")}),-1.0]])]});
            extrude(context, id + "F6", {"entities" : qUnion([Q0]), "depth" : 19.05 * mm, "offsetDistance" : 25.4 * mm});
        }
        {
            var Q0;
            Q0=makeQuery(id+"F0.imprint","IMPRINT",FACE,{"disambiguationData":[TD([[makeQuery(id+"F0.imprint","IMPRINT",EDGE,{"derivedFrom":sQuery(id+"F0.wireOp",EDGE,"E30")}),1.0]])]});
            extrude(context, id + "F7", {"entities" : qUnion([Q0]), "depth" : 19.05 * mm, "offsetDistance" : 25.4 * mm});
        }
        {
            var Q0;
            Q0=makeQuery(id+"F0.imprint","IMPRINT",FACE,{"disambiguationData":[TD([[makeQuery(id+"F0.imprint","IMPRINT",EDGE,{"derivedFrom":sQuery(id+"F0.wireOp",EDGE,"E34")}),1.0]])]});
            extrude(context, id + "F8", {"entities" : qUnion([Q0]), "depth" : 19.05 * mm, "offsetDistance" : 25.4 * mm});
        }
        {
            var Q0;
            Q0=makeQuery(id+"F0.imprint","IMPRINT",FACE,{"disambiguationData":[TD([[makeQuery(id+"F0.imprint","IMPRINT",EDGE,{"derivedFrom":sQuery(id+"F0.wireOp",EDGE,"E0")}),1.0]])]});
            extrude(context, id + "F9", {"entities" : qUnion([Q0]), "depth" : 19.05 * mm, "offsetDistance" : 25.4 * mm});
        }
        {
            var Q0;
            Q0=makeQuery(id+"F5.opExtrude","CAP_FACE",FACE,{"disambiguationData":[OSD([sQuery(id+"F0.wireOp",EDGE,"E262"),sQuery(id+"F0.wireOp",EDGE,"E263"),sQuery(id+"F0.wireOp",EDGE,"E264"),sQuery(id+"F0.wireOp",EDGE,"E265"),sQuery(id+"F0.wireOp",EDGE,"E266"),sQuery(id+"F0.wireOp",EDGE,"E267"),sQuery(id+"F0.wireOp",EDGE,"E268"),sQuery(id+"F0.wireOp",EDGE,"E269"),sQuery(id+"F0.wireOp",EDGE,"E270"),sQuery(id+"F0.wireOp",EDGE,"E271"),sQuery(id+"F0.wireOp",EDGE,"E272"),sQuery(id+"F0.wireOp",EDGE,"E273"),sQuery(id+"F0.wireOp",EDGE,"E274"),sQuery(id+"F0.wireOp",EDGE,"E275"),sQuery(id+"F0.wireOp",EDGE,"E284"),sQuery(id+"F0.wireOp",EDGE,"E285"),sQuery(id+"F0.wireOp",EDGE,"E286"),sQuery(id+"F0.wireOp",EDGE,"E287"),sQuery(id+"F0.wireOp",EDGE,"E288"),sQuery(id+"F0.wireOp",EDGE,"E289"),sQuery(id+"F0.wireOp",EDGE,"E290"),sQuery(id+"F0.wireOp",EDGE,"E291")])],"isStart":false});
            var sketch = newSketch(context, id + "F10", { "sketchPlane" : qUnion([Q0])});
            skLineSegment(sketch, "E403.bottom", {"start": v(-200.65, -454.5) * mm, "end": v(-99.9, -454.5) * mm});
            skLineSegment(sketch, "E403.top", {"start": v(-200.65, -521.67) * mm, "end": v(-99.9, -521.67) * mm});
            skLineSegment(sketch, "E403.left", {"start": v(-200.65, -454.5) * mm, "end": v(-200.65, -521.67) * mm});
            skLineSegment(sketch, "E403.right", {"start": v(-99.9, -454.5) * mm, "end": v(-99.9, -521.67) * mm});
            skSolve(sketch);
        }
        {
            var Q0;
            Q0=makeQuery(id+"F10.imprint","IMPRINT",FACE,{"disambiguationData":[TD([[makeQuery(id+"F10.imprint","IMPRINT",EDGE,{"derivedFrom":sQuery(id+"F10.wireOp",EDGE,"E403.bottom")}),-1.0]])]});
            extrude(context, id + "F11", {"entities" : qUnion([Q0]), "operationType" : NewBodyOperationType.REMOVE, "oppositeDirection" : true, "depth" : 12.7 * mm, "offsetDistance" : 25.4 * mm});
        }
    });
